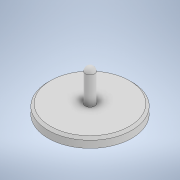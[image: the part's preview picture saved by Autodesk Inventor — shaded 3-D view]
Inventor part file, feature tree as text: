
AUTODESK INVENTOR PART (.ipt)
format: ipt  version: 2022 (Build 260153000, 153)  size: 115,712 bytes
history: native  units: mm
features: extrude x2, other x1, sketch x1, chamfer x1, fillet x1
ambient origin geometry x8: Origin, YZ Plane, XZ Plane, XY Plane, X Axis, Y Axis, Z Axis, Center Point
bodies: Body1 (feature_tree)
feature tree (6):
  other  "Sólido1"
  sketch  "Boceto1"  dims[d0=18.0mm d1=2.0mm d2=0.0mm d3=9.0mm d4=0.0mm d5=0.5mm d6=2.0mm d7=45.0deg d8=1.0mm]
  extrude  "Extrusión1"  Depth=2.0mm TaperAngle=0.0deg
  extrude  "Extrusión2"  Depth=9.0mm TaperAngle=0.0deg
  chamfer  "Chaflán1"  Distance=2.0mm Angle=45.0deg
  fillet  "Empalme1"  Radius=1.0mm
